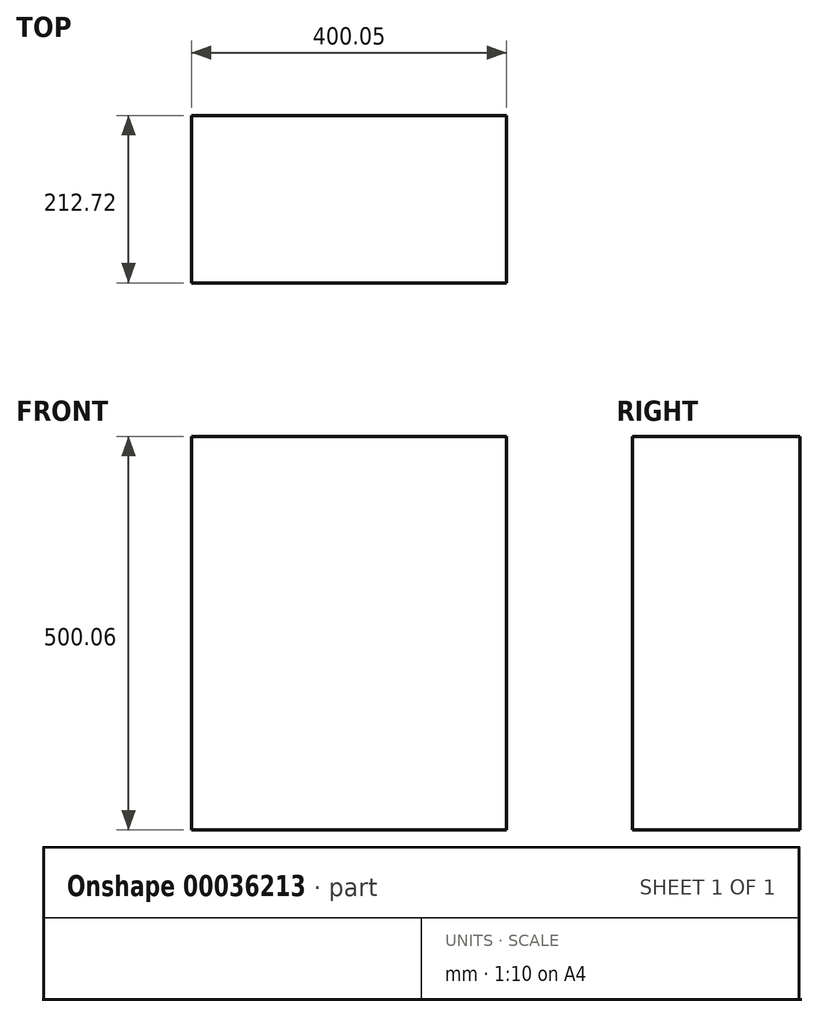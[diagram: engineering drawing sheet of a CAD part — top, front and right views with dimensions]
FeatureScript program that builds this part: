
annotation { "Feature Type Name" : "Feature", "Feature Type Description" : "" }
export const myFeature = defineFeature(function(context is Context, id is Id, definition is map)
    precondition{}
    {
        {
            var Q0;
            Q0=qCreatedBy(makeId("Front.planeOp"),FACE);
            var sketch = newSketch(context, id + "F0", { "sketchPlane" : qUnion([Q0])});
            skLineSegment(sketch, "E0.bottom", {"start": v(0, 0) * mm, "end": v(400.05, 0) * mm});
            skLineSegment(sketch, "E0.top", {"start": v(0, 500.06) * mm, "end": v(400.05, 500.06) * mm});
            skLineSegment(sketch, "E0.left", {"start": v(0, 0) * mm, "end": v(0, 500.06) * mm});
            skLineSegment(sketch, "E0.right", {"start": v(400.05, 0) * mm, "end": v(400.05, 500.06) * mm});
            skSolve(sketch);
        }
        {
            var Q0;
            Q0=qSketchRegion(id+"F0",true);
            extrude(context, id + "F1", {"entities" : qUnion([Q0]), "depth" : 212.72 * mm});
        }
    });
